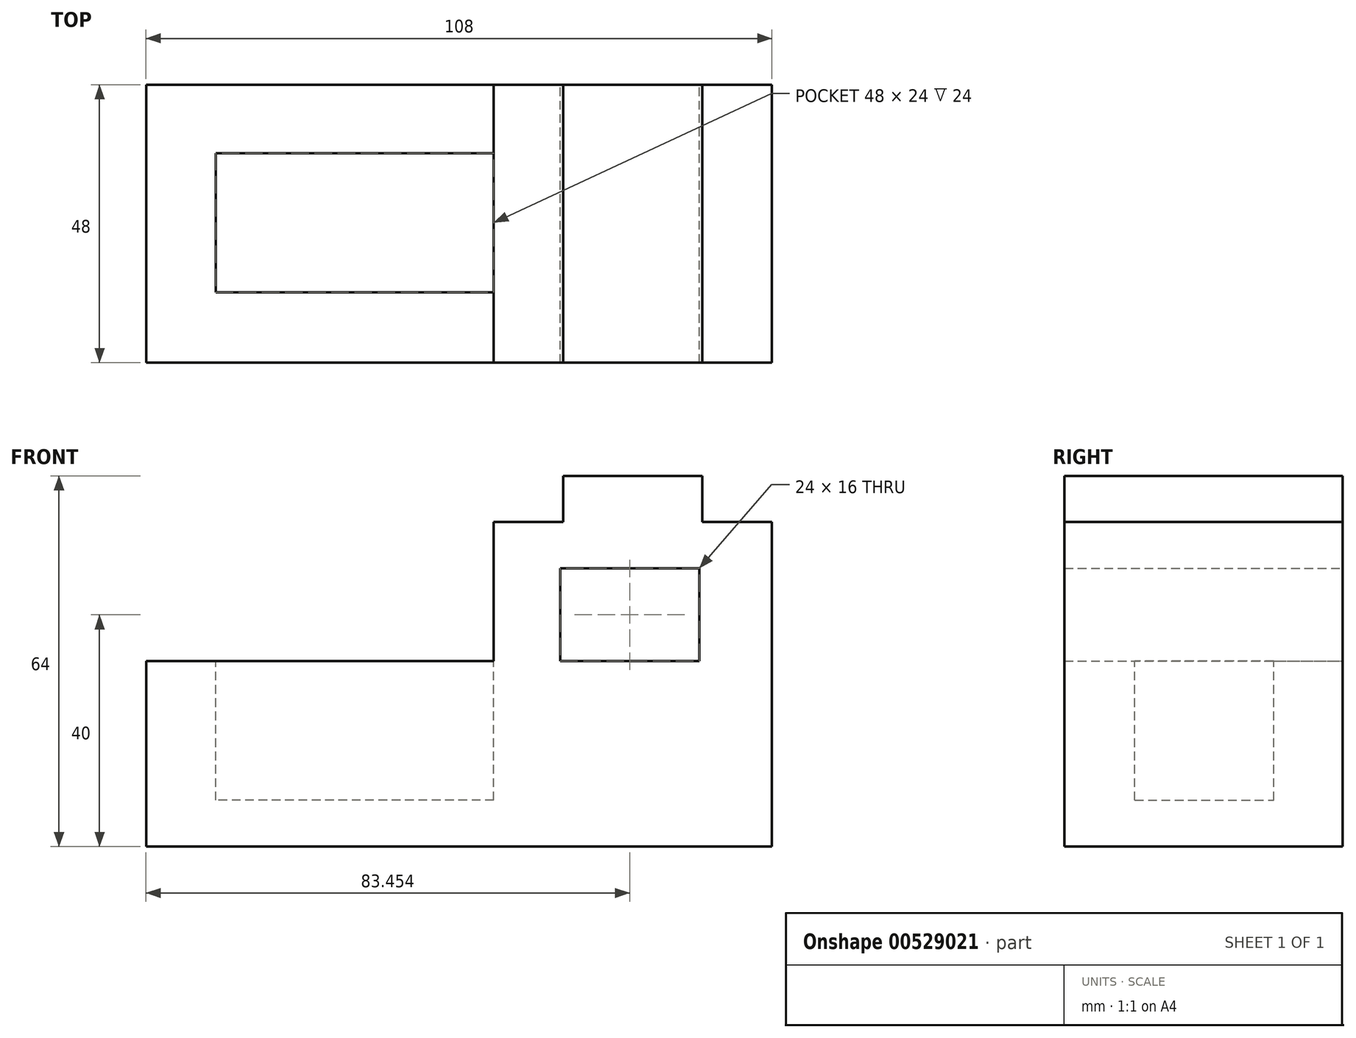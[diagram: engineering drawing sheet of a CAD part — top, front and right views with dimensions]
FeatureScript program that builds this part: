
annotation { "Feature Type Name" : "Feature", "Feature Type Description" : "" }
export const myFeature = defineFeature(function(context is Context, id is Id, definition is map)
    precondition{}
    {
        {
            var Q0;
            Q0=qCreatedBy(makeId("Front.planeOp"),FACE);
            var sketch = newSketch(context, id + "F0", { "sketchPlane" : qUnion([Q0])});
            skLineSegment(sketch, "E0", {"start": v(-53.63, 0) * mm, "end": v(54.37, 0) * mm});
            skLineSegment(sketch, "E1", {"start": v(54.37, 0) * mm, "end": v(54.37, 56) * mm});
            skLineSegment(sketch, "E2", {"start": v(54.37, 56) * mm, "end": v(42.37, 56) * mm});
            skLineSegment(sketch, "E3", {"start": v(42.37, 56) * mm, "end": v(42.37, 64) * mm});
            skLineSegment(sketch, "E4", {"start": v(42.37, 64) * mm, "end": v(18.37, 64) * mm});
            skLineSegment(sketch, "E5", {"start": v(18.37, 64) * mm, "end": v(18.37, 56) * mm});
            skLineSegment(sketch, "E6", {"start": v(18.37, 56) * mm, "end": v(6.37, 56) * mm});
            skLineSegment(sketch, "E7", {"start": v(-53.63, 0) * mm, "end": v(-53.63, 32) * mm});
            skLineSegment(sketch, "E8", {"start": v(-53.63, 32) * mm, "end": v(6.37, 32) * mm});
            skLineSegment(sketch, "E9", {"start": v(6.37, 32) * mm, "end": v(6.37, 56) * mm});
            skPoint(sketch, "E10.startSnap0", {"position": v(54.37, 28) * mm});
            skLineSegment(sketch, "E11", {"start": v(41.82, 32) * mm, "end": v(41.82, 48) * mm});
            skLineSegment(sketch, "E12", {"start": v(41.82, 48) * mm, "end": v(17.82, 48) * mm});
            skLineSegment(sketch, "E13", {"start": v(17.82, 48) * mm, "end": v(17.82, 32) * mm});
            skLineSegment(sketch, "E14", {"start": v(41.82, 32) * mm, "end": v(17.82, 32) * mm});
            skSolve(sketch);
        }
        {
            var Q0;
            Q0 = qSketchRegion(id + "F0", true);
            extrude(context, id + "F1", {"entities" : qUnion([Q0]), "depth" : 48 * mm, "offsetDistance" : 25 * mm});
        }
        {
            var Q0;
            Q0=makeQuery(id+"F1.opExtrude","SWEPT_FACE",FACE,{"disambiguationData":[OSD([sQuery(id+"F0.wireOp",EDGE,"E8")])]});
            var sketch = newSketch(context, id + "F2", { "sketchPlane" : qUnion([Q0])});
            skLineSegment(sketch, "E15", {"start": v(6.37, -11.87) * mm, "end": v(-41.63, -11.87) * mm});
            skLineSegment(sketch, "E16", {"start": v(-41.63, -11.87) * mm, "end": v(-41.63, -35.87) * mm});
            skLineSegment(sketch, "E17", {"start": v(-41.63, -35.87) * mm, "end": v(6.37, -35.87) * mm});
            skSolve(sketch);
        }
        {
            var Q0;
            {var subQ0=sQuery(id+"F2.wireOp",EDGE,"E15");Q0=makeQuery(id+"F2.imprint","IMPRINT",FACE,{"disambiguationData":[TD([[makeQuery(id+"F2.imprint","IMPRINT",EDGE,{"derivedFrom":subQ0}),1.0]])]});}
            extrude(context, id + "F3", {"entities" : qUnion([Q0]), "operationType" : NewBodyOperationType.REMOVE, "oppositeDirection" : true, "depth" : 24 * mm, "offsetDistance" : 25 * mm});
        }
    });
